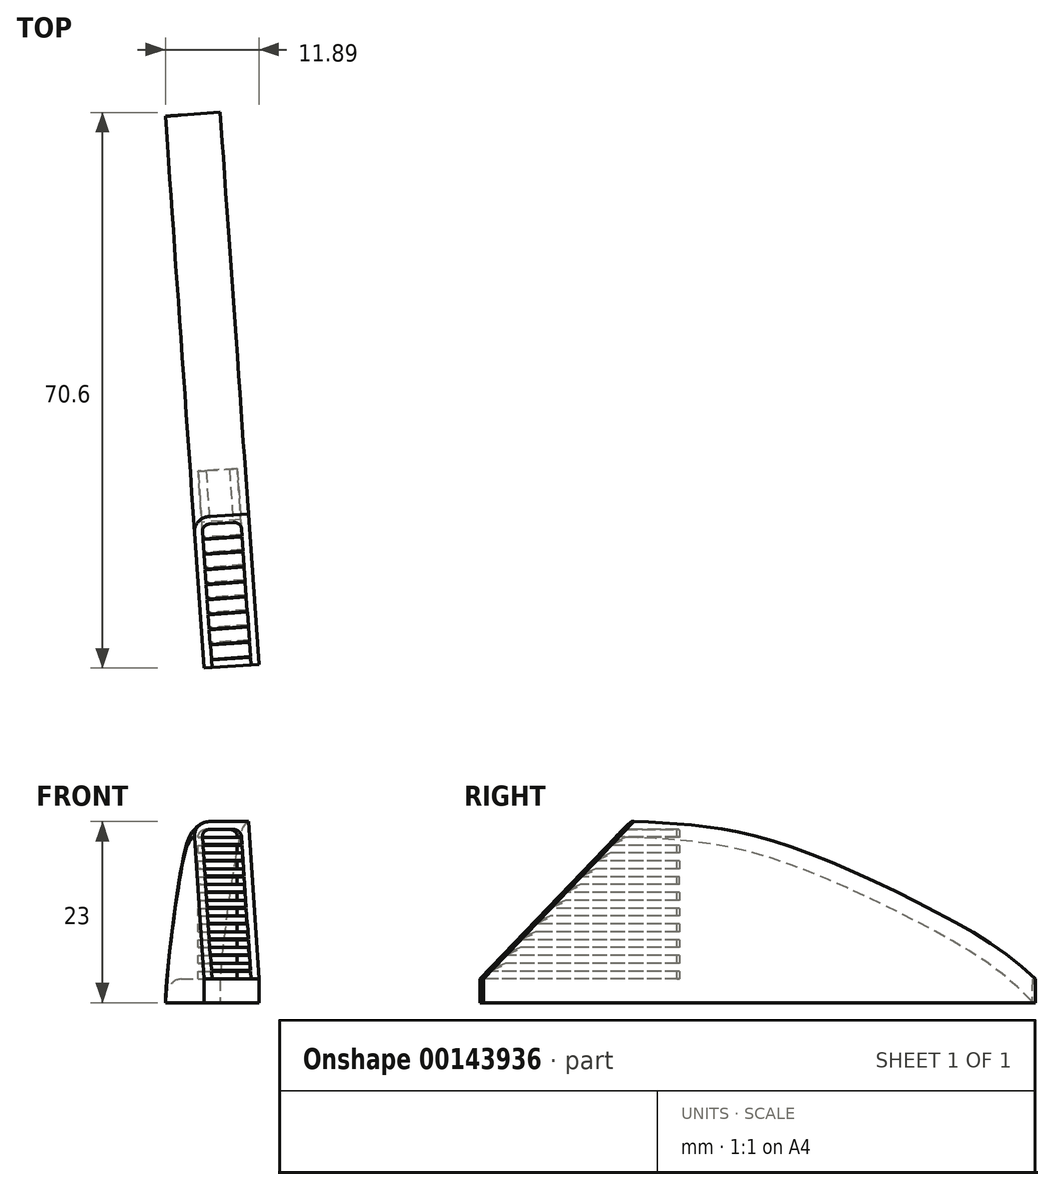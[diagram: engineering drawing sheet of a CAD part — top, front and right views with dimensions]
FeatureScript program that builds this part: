
annotation { "Feature Type Name" : "Feature", "Feature Type Description" : "" }
export const myFeature = defineFeature(function(context is Context, id is Id, definition is map)
    precondition{}
    {
        {
            var Q0;
            Q0=qCreatedBy(makeId("Top.planeOp"),FACE);
            var sketch = newSketch(context, id + "F0", { "sketchPlane" : qUnion([Q0])});
            skLineSegment(sketch, "E0", {"start": v(-28.15, -11.86) * mm, "end": v(-23.23, 58.25) * mm});
            skLineSegment(sketch, "E1", {"start": v(-30.2, 58.74) * mm, "end": v(-35.12, -11.37) * mm});
            skLineSegment(sketch, "E2", {"start": v(-23.23, 58.25) * mm, "end": v(-30.2, 58.74) * mm});
            skLineSegment(sketch, "E3", {"start": v(-28.15, -11.86) * mm, "end": v(-35.12, -11.37) * mm});
            skSolve(sketch);
        }
        {
            var Q0;
            Q0=qSketchRegion(id+"F0",true);
            extrude(context, id + "F1", {"entities" : qUnion([Q0]), "depth" : 3 * mm});
        }
        {
            var Q0;
            Q0=makeQuery(id+"F1.opExtrude","CAP_FACE",FACE,{"disambiguationData":[OSD([sQuery(id+"F0.wireOp",EDGE,"mfbUUH89-GhNW-xkRt-vmny-iapurk2HKPIS"),sQuery(id+"F0.wireOp",EDGE,"E0"),sQuery(id+"F0.wireOp",EDGE,"JSxFqMj3-m5DG-nVDL-T3pK-i0W8c60JwMJz"),sQuery(id+"F0.wireOp",EDGE,"E1"),sQuery(id+"F0.wireOp",EDGE,"E2"),sQuery(id+"F0.wireOp",EDGE,"Zva8UKAF-Idc9-vliP-45KG-4Emh3L01odaY")])],"isStart":false});
            var sketch = newSketch(context, id + "F2", { "sketchPlane" : qUnion([Q0])});
            skLineSegment(sketch, "E4", {"start": v(-30.2, 58.74) * mm, "end": v(-30.2, 58.74) * mm});
            skLineSegment(sketch, "E5", {"start": v(-30.2, 58.74) * mm, "end": v(-35.12, -11.37) * mm});
            skLineSegment(sketch, "E6", {"start": v(-35.12, -11.37) * mm, "end": v(-28.15, -11.86) * mm});
            skLineSegment(sketch, "E7", {"start": v(-30.2, 58.74) * mm, "end": v(-23.23, 58.25) * mm});
            skLineSegment(sketch, "E8", {"start": v(-23.23, 58.25) * mm, "end": v(-28.15, -11.86) * mm});
            skSolve(sketch);
        }
        {
            var Q0;
            Q0=qSketchRegion(id+"F2",true);
            extrude(context, id + "F3", {"entities" : qUnion([Q0]), "operationType" : NewBodyOperationType.ADD, "depth" : 20 * mm});
        }
        {
            var Q0;
            Q0=makeQuery(id+"F3.boolean.opBoolean","MERGE",FACE,{"derivedFrom":[makeQuery(id+"F1.opExtrude","SWEPT_FACE",FACE,{"disambiguationData":[OSD([sQuery(id+"F0.wireOp",EDGE,"E1")])]}),makeQuery(id+"F3.opExtrude","SWEPT_FACE",FACE,{"disambiguationData":[OSD([sQuery(id+"F2.wireOp",EDGE,"E5")])]})]});
            var sketch = newSketch(context, id + "F4", { "sketchPlane" : qUnion([Q0])});
            skLineSegment(sketch, "E9", {"start": v(13.8, 3) * mm, "end": v(-5.36, 23) * mm});
            skFitSpline(sketch, "E10", {"points": [v(-5.36, 23) * mm, v(-13.54, 22.46) * mm, v(-24.86, 19.96) * mm, v(-43.34, 11.76) * mm, v(-56.48, 3) * mm], "startDerivative": vector(-41.6, -1.3) * mm, "endDerivative": vector(-39.84, -39.3) * mm});
            skLineSegment(sketch, "E11", {"start": v(-56.48, 3) * mm, "end": v(-61.7, 3) * mm});
            skLineSegment(sketch, "E12", {"start": v(-61.7, 3) * mm, "end": v(-61.7, 25.73) * mm});
            skLineSegment(sketch, "E13", {"start": v(-61.7, 25.73) * mm, "end": v(18.56, 25.73) * mm});
            skLineSegment(sketch, "E14", {"start": v(18.56, 25.73) * mm, "end": v(13.8, 3) * mm});
            skSolve(sketch);
        }
        {
            var Q0;
            Q0=qSketchRegion(id+"F4",true);
            extrude(context, id + "F5", {"entities" : qUnion([Q0]), "operationType" : NewBodyOperationType.REMOVE, "oppositeDirection" : true, "depth" : 25 * mm});
        }
        {
            var Q0;
            Q0=makeQuery(id+"F5.boolean.opBoolean","COPY",EDGE,{"derivedFrom":makeQuery(id+"F5.opExtrude","CAP_EDGE",EDGE,{"disambiguationData":[OSD([sQuery(id+"F4.wireOp",EDGE,"E10")])],"isStart":true})});
            var Q1;
            Q1=makeQuery(id+"F5.boolean.opBoolean","INTERSECT",EDGE,{"derivedFrom":[makeQuery(id+"F3.boolean.opBoolean","MERGE",FACE,{"derivedFrom":[makeQuery(id+"F1.opExtrude","SWEPT_FACE",FACE,{"disambiguationData":[OSD([sQuery(id+"F0.wireOp",EDGE,"E0")])]}),makeQuery(id+"F3.opExtrude","SWEPT_FACE",FACE,{"disambiguationData":[OSD([sQuery(id+"F2.wireOp",EDGE,"E8")])]})]}),makeQuery(id+"F5.opExtrude","SWEPT_FACE",FACE,{"disambiguationData":[OSD([sQuery(id+"F4.wireOp",EDGE,"E10")])]})]});
            fillet(context, id + "F6", {"entities" : qUnion([Q0, Q1]), "radius" : 2 * mm, "tangentPropagation" : true, "allowEdgeOverflow" : false});
        }
        {
            var Q0;
            Q0=makeQuery(id+"F3.boolean.opBoolean","MERGE",FACE,{"derivedFrom":[makeQuery(id+"F1.opExtrude","SWEPT_FACE",FACE,{"disambiguationData":[OSD([sQuery(id+"F0.wireOp",EDGE,"E3")])]}),makeQuery(id+"F3.opExtrude","SWEPT_FACE",FACE,{"disambiguationData":[OSD([sQuery(id+"F2.wireOp",EDGE,"E6")])]})]});
            var sketch = newSketch(context, id + "F7", { "sketchPlane" : qUnion([Q0])});
            skLineSegment(sketch, "E15.0", {"start": v(-33.23, 4) * mm, "end": v(-28.25, 4) * mm});
            skFitSpline(sketch, "E15.1", {"points": [v(-28.25, 21.06) * mm, v(-28.25, 21.11) * mm, v(-28.26, 21.21) * mm, v(-28.3, 21.37) * mm, v(-28.38, 21.52) * mm, v(-28.48, 21.66) * mm, v(-28.62, 21.8) * mm, v(-28.86, 21.94) * mm, v(-29.1, 22) * mm, v(-29.25, 22) * mm]});
            skLineSegment(sketch, "E15.2", {"start": v(-29.25, 22) * mm, "end": v(-32.23, 22) * mm});
            skLineSegment(sketch, "E15.3", {"start": v(-28.25, 5) * mm, "end": v(-28.25, 6) * mm});
            skFitSpline(sketch, "E15.4", {"points": [v(-32.23, 22) * mm, v(-32.32, 22) * mm, v(-32.43, 21.99) * mm, v(-32.58, 21.94) * mm, v(-32.72, 21.89) * mm, v(-32.87, 21.8) * mm, v(-33.05, 21.62) * mm, v(-33.2, 21.37) * mm, v(-33.23, 21.16) * mm, v(-33.23, 21.06) * mm]});
            skLineSegment(sketch, "E15.5", {"start": v(-33.23, 21.06) * mm, "end": v(-33.23, 21) * mm});
            skLineSegment(sketch, "E16.0", {"start": v(-33.23, 5) * mm, "end": v(-28.25, 5) * mm});
            skLineSegment(sketch, "E17.0.1.0", {"start": v(-33.23, 6) * mm, "end": v(-28.25, 6) * mm});
            skLineSegment(sketch, "E17.0.2.0", {"start": v(-33.23, 7) * mm, "end": v(-28.25, 7) * mm});
            skLineSegment(sketch, "E17.0.3.0", {"start": v(-33.23, 8) * mm, "end": v(-28.25, 8) * mm});
            skLineSegment(sketch, "E17.0.4.0", {"start": v(-33.23, 9) * mm, "end": v(-28.25, 9) * mm});
            skLineSegment(sketch, "E17.0.5.0", {"start": v(-33.23, 10) * mm, "end": v(-28.25, 10) * mm});
            skLineSegment(sketch, "E17.0.6.0", {"start": v(-33.23, 11) * mm, "end": v(-28.25, 11) * mm});
            skLineSegment(sketch, "E17.0.7.0", {"start": v(-33.23, 12) * mm, "end": v(-28.25, 12) * mm});
            skLineSegment(sketch, "E17.0.8.0", {"start": v(-33.23, 13) * mm, "end": v(-28.25, 13) * mm});
            skLineSegment(sketch, "E17.0.9.0", {"start": v(-33.23, 14) * mm, "end": v(-28.25, 14) * mm});
            skLineSegment(sketch, "E17.0.10.0", {"start": v(-33.23, 15) * mm, "end": v(-28.25, 15) * mm});
            skLineSegment(sketch, "E17.0.11.0", {"start": v(-33.23, 16) * mm, "end": v(-28.25, 16) * mm});
            skLineSegment(sketch, "E17.0.12.0", {"start": v(-33.23, 17) * mm, "end": v(-28.25, 17) * mm});
            skLineSegment(sketch, "E17.0.13.0", {"start": v(-33.23, 18) * mm, "end": v(-28.25, 18) * mm});
            skLineSegment(sketch, "E17.0.14.0", {"start": v(-33.23, 19) * mm, "end": v(-28.25, 19) * mm});
            skLineSegment(sketch, "E17.0.15.0", {"start": v(-33.23, 20) * mm, "end": v(-28.25, 20) * mm});
            skLineSegment(sketch, "E17.0.16.0", {"start": v(-33.23, 21) * mm, "end": v(-28.25, 21) * mm});
            skLineSegment(sketch, "E17.direction2", {"start": v(-33.23, 5) * mm, "end": v(-33.23, 6) * mm, "construction": true});
            skLineSegment(sketch, "E18.trimOffspring", {"start": v(-33.23, 20) * mm, "end": v(-33.23, 19) * mm});
            skLineSegment(sketch, "E19.trimOffspring", {"start": v(-28.25, 21) * mm, "end": v(-28.25, 21.06) * mm});
            skLineSegment(sketch, "E20.trimOffspring", {"start": v(-28.25, 19) * mm, "end": v(-28.25, 20) * mm});
            skLineSegment(sketch, "E21.trimOffspring", {"start": v(-33.23, 18) * mm, "end": v(-33.23, 17) * mm});
            skLineSegment(sketch, "E22.trimOffspring", {"start": v(-28.25, 17) * mm, "end": v(-28.25, 18) * mm});
            skLineSegment(sketch, "E23.trimOffspring", {"start": v(-28.25, 15) * mm, "end": v(-28.25, 16) * mm});
            skLineSegment(sketch, "E24.trimOffspring", {"start": v(-33.23, 14) * mm, "end": v(-33.23, 13) * mm});
            skLineSegment(sketch, "E25.trimOffspring", {"start": v(-28.25, 13) * mm, "end": v(-28.25, 14) * mm});
            skLineSegment(sketch, "E26.trimOffspring", {"start": v(-33.23, 12) * mm, "end": v(-33.23, 11) * mm});
            skLineSegment(sketch, "E27", {"start": v(-33.23, 15) * mm, "end": v(-33.23, 16) * mm});
            skLineSegment(sketch, "E28.trimOffspring", {"start": v(-28.25, 11) * mm, "end": v(-28.25, 12) * mm});
            skLineSegment(sketch, "E29.trimOffspring", {"start": v(-33.23, 10) * mm, "end": v(-33.23, 9) * mm});
            skLineSegment(sketch, "E30.trimOffspring", {"start": v(-28.25, 9) * mm, "end": v(-28.25, 10) * mm});
            skLineSegment(sketch, "E31.trimOffspring", {"start": v(-33.23, 8) * mm, "end": v(-33.23, 7) * mm});
            skLineSegment(sketch, "E32.trimOffspring", {"start": v(-28.25, 7) * mm, "end": v(-28.25, 8) * mm});
            skLineSegment(sketch, "E33.trimOffspring", {"start": v(-33.23, 6) * mm, "end": v(-33.23, 5) * mm});
            skLineSegment(sketch, "E34", {"start": v(-33.23, 4) * mm, "end": v(-33.23, 3) * mm});
            skLineSegment(sketch, "E35", {"start": v(-33.23, 3) * mm, "end": v(-28.25, 3) * mm});
            skLineSegment(sketch, "E36", {"start": v(-28.25, 3) * mm, "end": v(-28.25, 4) * mm});
            skSolve(sketch);
        }
        {
            var Q0;
            Q0=qSketchRegion(id+"F7",true);
            extrude(context, id + "F8", {"entities" : qUnion([Q0]), "operationType" : NewBodyOperationType.REMOVE, "oppositeDirection" : true, "depth" : 25 * mm});
        }
        {
            var Q0;
            Q0=makeQuery(id+"F8.boolean.opBoolean","INTERSECT",EDGE,{"derivedFrom":[makeQuery(id+"F5.boolean.opBoolean","COPY",FACE,{"derivedFrom":makeQuery(id+"F5.opExtrude","SWEPT_FACE",FACE,{"disambiguationData":[OSD([sQuery(id+"F4.wireOp",EDGE,"E9")])]})}),makeQuery(id+"F8.opExtrude","SWEPT_FACE",FACE,{"disambiguationData":[OSD([sQuery(id+"F7.wireOp",EDGE,"E17.0.16.0")])]})]});
            var Q1;
            Q1=makeQuery(id+"F8.boolean.opBoolean","INTERSECT",EDGE,{"derivedFrom":[makeQuery(id+"F5.boolean.opBoolean","COPY",FACE,{"derivedFrom":makeQuery(id+"F5.opExtrude","SWEPT_FACE",FACE,{"disambiguationData":[OSD([sQuery(id+"F4.wireOp",EDGE,"E9")])]})}),makeQuery(id+"F8.opExtrude","SWEPT_FACE",FACE,{"disambiguationData":[OSD([sQuery(id+"F7.wireOp",EDGE,"E17.0.14.0")])]})]});
            var Q2;
            Q2=makeQuery(id+"F8.boolean.opBoolean","INTERSECT",EDGE,{"derivedFrom":[makeQuery(id+"F5.boolean.opBoolean","COPY",FACE,{"derivedFrom":makeQuery(id+"F5.opExtrude","SWEPT_FACE",FACE,{"disambiguationData":[OSD([sQuery(id+"F4.wireOp",EDGE,"E9")])]})}),makeQuery(id+"F8.opExtrude","SWEPT_FACE",FACE,{"disambiguationData":[OSD([sQuery(id+"F7.wireOp",EDGE,"E17.0.12.0")])]})]});
            var Q3;
            Q3=makeQuery(id+"F8.boolean.opBoolean","INTERSECT",EDGE,{"derivedFrom":[makeQuery(id+"F5.boolean.opBoolean","COPY",FACE,{"derivedFrom":makeQuery(id+"F5.opExtrude","SWEPT_FACE",FACE,{"disambiguationData":[OSD([sQuery(id+"F4.wireOp",EDGE,"E9")])]})}),makeQuery(id+"F8.opExtrude","SWEPT_FACE",FACE,{"disambiguationData":[OSD([sQuery(id+"F7.wireOp",EDGE,"E17.0.10.0")])]})]});
            var Q4;
            Q4=makeQuery(id+"F8.boolean.opBoolean","INTERSECT",EDGE,{"derivedFrom":[makeQuery(id+"F5.boolean.opBoolean","COPY",FACE,{"derivedFrom":makeQuery(id+"F5.opExtrude","SWEPT_FACE",FACE,{"disambiguationData":[OSD([sQuery(id+"F4.wireOp",EDGE,"E9")])]})}),makeQuery(id+"F8.opExtrude","SWEPT_FACE",FACE,{"disambiguationData":[OSD([sQuery(id+"F7.wireOp",EDGE,"E17.0.8.0")])]})]});
            var Q5;
            Q5=makeQuery(id+"F8.boolean.opBoolean","INTERSECT",EDGE,{"derivedFrom":[makeQuery(id+"F5.boolean.opBoolean","COPY",FACE,{"derivedFrom":makeQuery(id+"F5.opExtrude","SWEPT_FACE",FACE,{"disambiguationData":[OSD([sQuery(id+"F4.wireOp",EDGE,"E9")])]})}),makeQuery(id+"F8.opExtrude","SWEPT_FACE",FACE,{"disambiguationData":[OSD([sQuery(id+"F7.wireOp",EDGE,"E17.0.6.0")])]})]});
            var Q6;
            Q6=makeQuery(id+"F8.boolean.opBoolean","INTERSECT",EDGE,{"derivedFrom":[makeQuery(id+"F5.boolean.opBoolean","COPY",FACE,{"derivedFrom":makeQuery(id+"F5.opExtrude","SWEPT_FACE",FACE,{"disambiguationData":[OSD([sQuery(id+"F4.wireOp",EDGE,"E9")])]})}),makeQuery(id+"F8.opExtrude","SWEPT_FACE",FACE,{"disambiguationData":[OSD([sQuery(id+"F7.wireOp",EDGE,"E17.0.4.0")])]})]});
            var Q7;
            Q7=makeQuery(id+"F8.boolean.opBoolean","INTERSECT",EDGE,{"derivedFrom":[makeQuery(id+"F5.boolean.opBoolean","COPY",FACE,{"derivedFrom":makeQuery(id+"F5.opExtrude","SWEPT_FACE",FACE,{"disambiguationData":[OSD([sQuery(id+"F4.wireOp",EDGE,"E9")])]})}),makeQuery(id+"F8.opExtrude","SWEPT_FACE",FACE,{"disambiguationData":[OSD([sQuery(id+"F7.wireOp",EDGE,"E17.0.2.0")])]})]});
            var Q8;
            Q8=makeQuery(id+"F8.boolean.opBoolean","INTERSECT",EDGE,{"derivedFrom":[makeQuery(id+"F5.boolean.opBoolean","COPY",FACE,{"derivedFrom":makeQuery(id+"F5.opExtrude","SWEPT_FACE",FACE,{"disambiguationData":[OSD([sQuery(id+"F4.wireOp",EDGE,"E9")])]})}),makeQuery(id+"F8.opExtrude","SWEPT_FACE",FACE,{"disambiguationData":[OSD([sQuery(id+"F7.wireOp",EDGE,"E16.0")])]})]});
            chamfer(context, id + "F9", {"entities" : qUnion([Q0, Q1, Q2, Q3, Q4, Q5, Q6, Q7, Q8]), "width" : 1.25 * mm, "tangentPropagation" : true});
        }
        {
            var Q0;
            Q0=makeQuery(id+"F1.opExtrude","SWEPT_BODY",BODY,{"disambiguationData":[OSD([sQuery(id+"F0.wireOp",EDGE,"E0"),sQuery(id+"F0.wireOp",EDGE,"E1"),sQuery(id+"F0.wireOp",EDGE,"E2"),sQuery(id+"F0.wireOp",EDGE,"E3")])]});
            var Q1;
            Q1=qCreatedBy(makeId("Right.planeOp"),FACE);
            mirror(context, id + "F10", {"entities" : qUnion([Q0]), "mirrorPlane" : qUnion([Q1])});
        }
        {
            var Q0;
            Q0=makeQuery(id+"F1.opExtrude","SWEPT_BODY",BODY,{"disambiguationData":[OSD([sQuery(id+"F0.wireOp",EDGE,"E0"),sQuery(id+"F0.wireOp",EDGE,"E1"),sQuery(id+"F0.wireOp",EDGE,"E2"),sQuery(id+"F0.wireOp",EDGE,"E3")])]});
            deleteBodies(context, id + "F11", {"entities" : qUnion([Q0])});
        }
    });
